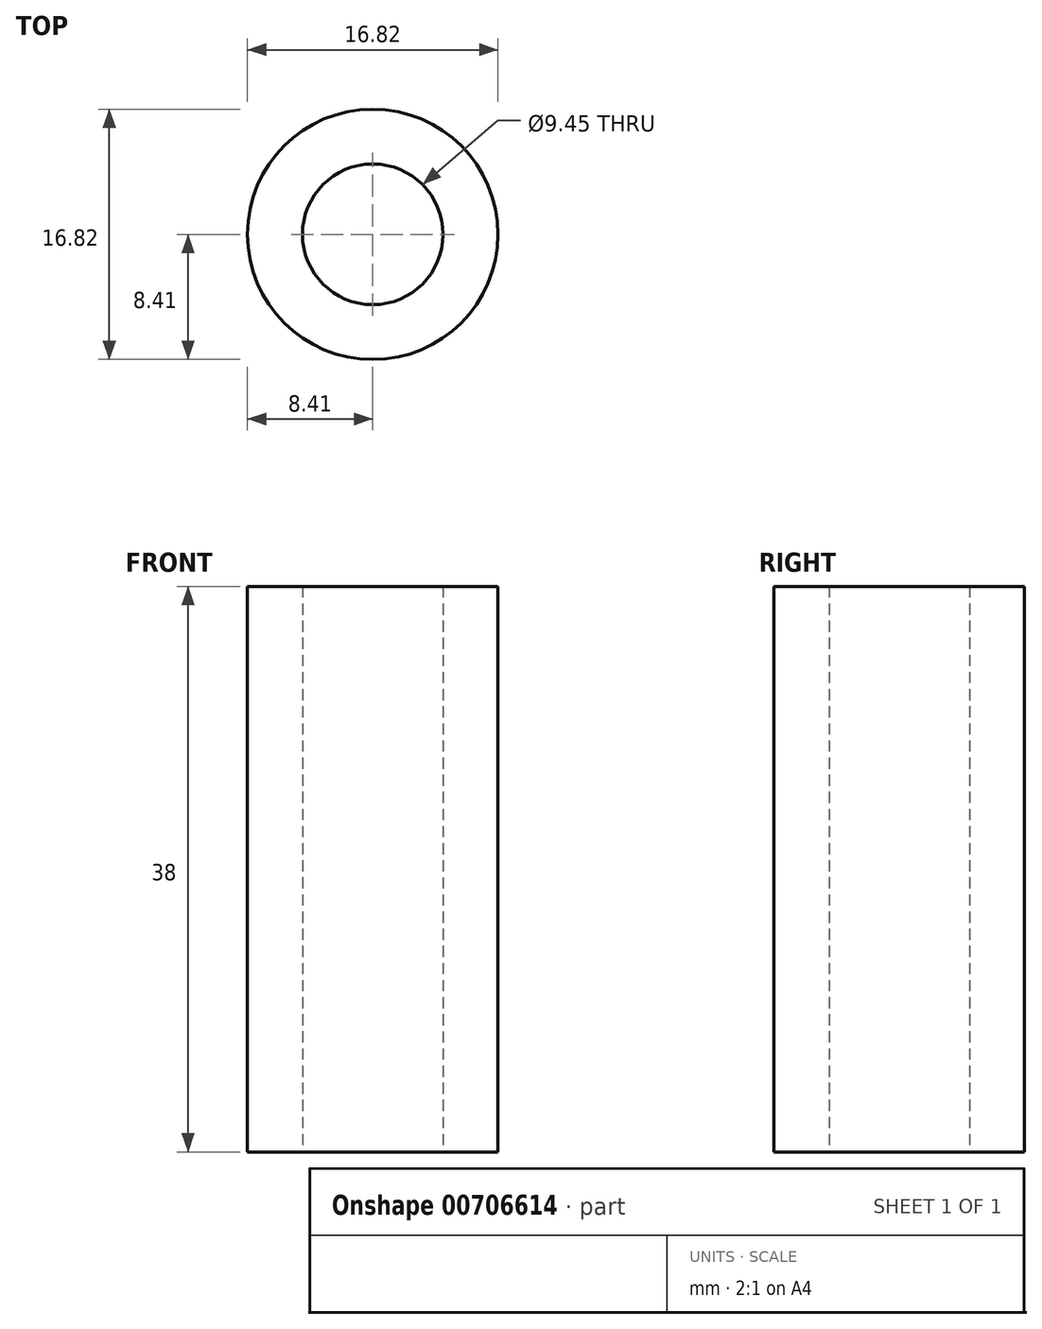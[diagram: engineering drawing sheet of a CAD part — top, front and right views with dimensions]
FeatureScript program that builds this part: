
annotation { "Feature Type Name" : "Feature", "Feature Type Description" : "" }
export const myFeature = defineFeature(function(context is Context, id is Id, definition is map)
    precondition{}
    {
        {
            var Q0;
            Q0=qCreatedBy(makeId("Top.planeOp"),FACE);
            var sketch = newSketch(context, id + "F0", { "sketchPlane" : qUnion([Q0])});
            skCircle(sketch, "E0", {"center": v(0, 0) * mm, "radius": 8.41 * mm});
            skCircle(sketch, "E1", {"center": v(0, 0) * mm, "radius": 4.72 * mm});
            skSolve(sketch);
        }
        {
            var Q0;
            Q0=makeQuery(id+"F0.imprint","IMPRINT",FACE,{"disambiguationData":[TD([[makeQuery(id+"F0.imprint","IMPRINT",EDGE,{"derivedFrom":sQuery(id+"F0.wireOp",EDGE,"E0")}),1.0]])]});
            extrude(context, id + "F1", {"entities" : qUnion([Q0]), "depth" : 38 * mm, "offsetDistance" : 25.4 * mm});
        }
    });
